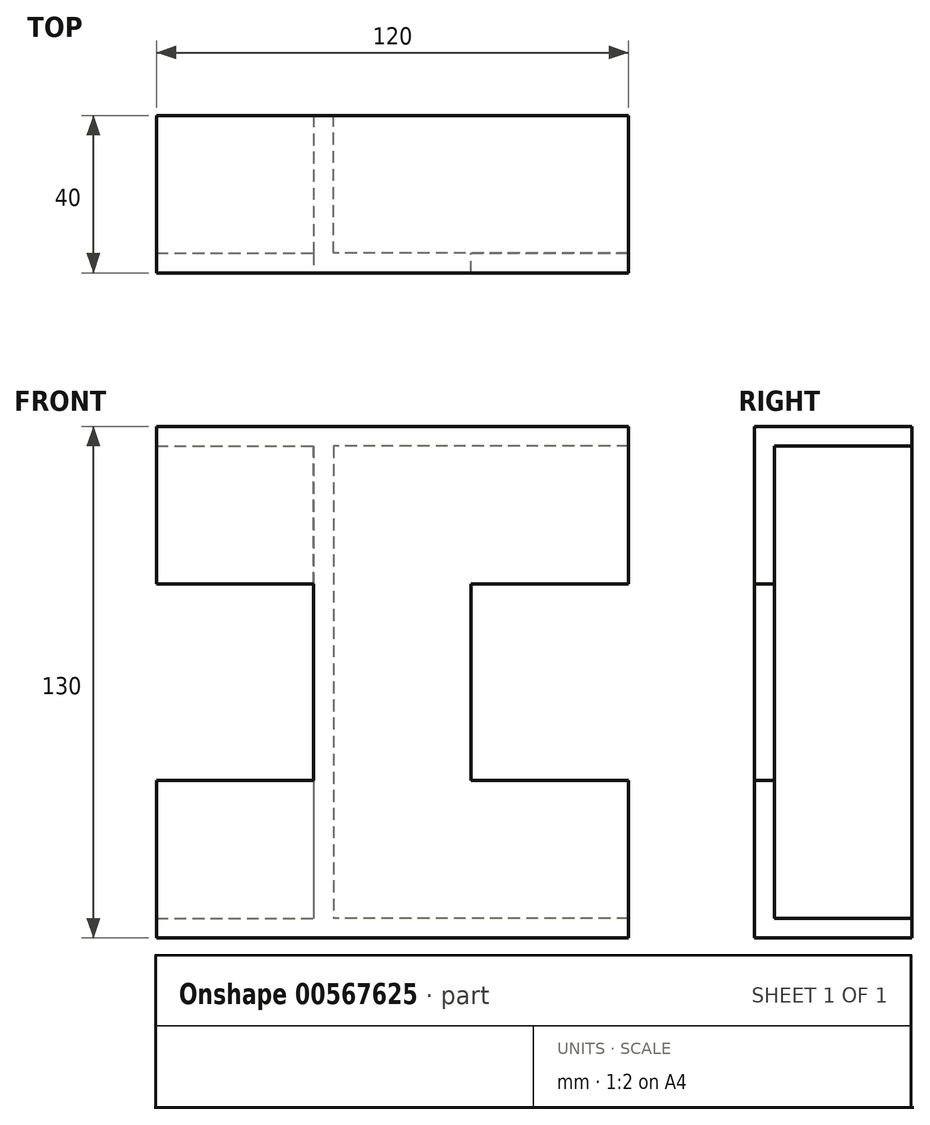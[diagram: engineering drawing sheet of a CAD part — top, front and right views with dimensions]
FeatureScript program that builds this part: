
annotation { "Feature Type Name" : "Feature", "Feature Type Description" : "" }
export const myFeature = defineFeature(function(context is Context, id is Id, definition is map)
    precondition{}
    {
        {
            var Q0;
            Q0=qCreatedBy(makeId("Right.planeOp"),FACE);
            var sketch = newSketch(context, id + "F0", { "sketchPlane" : qUnion([Q0])});
            skLineSegment(sketch, "E0", {"start": v(12.2, -34.52) * mm, "end": v(-27.8, -34.52) * mm});
            skLineSegment(sketch, "E1", {"start": v(-27.8, -34.52) * mm, "end": v(-27.8, -29.52) * mm});
            skLineSegment(sketch, "E2", {"start": v(-27.8, -29.52) * mm, "end": v(17.2, -29.52) * mm});
            skLineSegment(sketch, "E3", {"start": v(12.2, -34.52) * mm, "end": v(12.2, -29.52) * mm});
            skLineSegment(sketch, "E4", {"start": v(17.2, -29.52) * mm, "end": v(12.2, -29.52) * mm});
            skSolve(sketch);
        }
        {
            var Q0;
            Q0 = qSketchRegion(id + "F0", true);
            extrude(context, id + "F1", {"entities" : qUnion([Q0]), "depth" : 120 * mm, "offsetDistance" : 25 * mm});
        }
        {
            var Q0;
            Q0=makeQuery(id+"F1.opExtrude","SWEPT_FACE",FACE,{"disambiguationData":[OSD([sQuery(id+"F0.wireOp",EDGE,"E2"),sQuery(id+"F0.wireOp",EDGE,"E4")])]});
            var sketch = newSketch(context, id + "F2", { "sketchPlane" : qUnion([Q0])});
            skLineSegment(sketch, "E5", {"start": v(120, -27.8) * mm, "end": v(120, 12.2) * mm});
            skLineSegment(sketch, "E6", {"start": v(40, 12.2) * mm, "end": v(40, -27.8) * mm});
            skLineSegment(sketch, "E7", {"start": v(40, -27.8) * mm, "end": v(80, -27.8) * mm});
            skLineSegment(sketch, "E8", {"start": v(80, -27.8) * mm, "end": v(80, -22.8) * mm});
            skLineSegment(sketch, "E9", {"start": v(80, -22.8) * mm, "end": v(45, -22.8) * mm});
            skLineSegment(sketch, "E10", {"start": v(45, -22.8) * mm, "end": v(45, 12.2) * mm});
            skLineSegment(sketch, "E11", {"start": v(45, 12.2) * mm, "end": v(40, 12.2) * mm});
            skLineSegment(sketch, "E12", {"start": v(60, -27.8) * mm, "end": v(60, -7.8) * mm});
            skPoint(sketch, "E12.endSnap0", {"position": v(120, -7.8) * mm});
            skLineSegment(sketch, "E13", {"start": v(60, -7.8) * mm, "end": v(120, -7.8) * mm});
            skSolve(sketch);
        }
        {
            var Q0;
            Q0 = qSketchRegion(id + "F2", true);
            extrude(context, id + "F3", {"entities" : qUnion([Q0]), "operationType" : NewBodyOperationType.ADD, "depth" : 120 * mm, "offsetDistance" : 25 * mm});
        }
        {
            var Q0;
            Q0=makeQuery(id+"F3.opExtrude","CAP_FACE",FACE,{"disambiguationData":[OSD([sQuery(id+"F2.wireOp",EDGE,"E6"),sQuery(id+"F2.wireOp",EDGE,"E7"),sQuery(id+"F2.wireOp",EDGE,"E8"),sQuery(id+"F2.wireOp",EDGE,"E9"),sQuery(id+"F2.wireOp",EDGE,"E10"),sQuery(id+"F2.wireOp",EDGE,"E11")])],"isStart":false});
            var sketch = newSketch(context, id + "F4", { "sketchPlane" : qUnion([Q0])});
            skLineSegment(sketch, "E14.bottom", {"start": v(0, 12.2) * mm, "end": v(120, 12.2) * mm});
            skLineSegment(sketch, "E14.top", {"start": v(0, -27.8) * mm, "end": v(120, -27.8) * mm});
            skLineSegment(sketch, "E14.left", {"start": v(0, 12.2) * mm, "end": v(0, -27.8) * mm});
            skLineSegment(sketch, "E14.right", {"start": v(120, 12.2) * mm, "end": v(120, -27.8) * mm});
            skSolve(sketch);
        }
        {
            var Q0;
            Q0 = qSketchRegion(id + "F4", true);
            extrude(context, id + "F5", {"entities" : qUnion([Q0]), "operationType" : NewBodyOperationType.ADD, "depth" : 5 * mm, "offsetDistance" : 25 * mm});
        }
        {
            var Q0;
            {var subQ1=sQuery(id+"F0.wireOp",EDGE,"E4");var subQ2=sQuery(id+"F0.wireOp",EDGE,"E2");Q0=makeQuery(id+"F3.boolean.opBoolean","SPLIT",FACE,{"disambiguationData":[TD([makeQuery(id+"F3.opExtrude","SWEPT_FACE",FACE,{"disambiguationData":[OSD([sQuery(id+"F2.wireOp",EDGE,"E6")])]})])],"derivedFrom":makeQuery(id+"F1.opExtrude","SWEPT_FACE",FACE,{"disambiguationData":[OSD([subQ2,subQ1])]})});}
            var sketch = newSketch(context, id + "F6", { "sketchPlane" : qUnion([Q0])});
            skLineSegment(sketch, "E15", {"start": v(0, -27.8) * mm, "end": v(0, -22.8) * mm});
            skLineSegment(sketch, "E16", {"start": v(0, -22.8) * mm, "end": v(40, -22.8) * mm});
            skLineSegment(sketch, "E17", {"start": v(40, -22.8) * mm, "end": v(40, -27.8) * mm});
            skSolve(sketch);
        }
        {
            var Q0;
            Q0 = qSketchRegion(id + "F6", true);
            var Q1;
            Q1=makeQuery(id+"F6.imprint","IMPRINT",FACE,{"disambiguationData":[TD([[makeQuery(id+"F6.imprint","IMPRINT",EDGE,{"derivedFrom":sQuery(id+"F6.wireOp",EDGE,"E15")}),1.0]])]});
            var Q2;
            Q2=makeQuery(id+"F6.imprint","IMPRINT",FACE,{"disambiguationData":[TD([[makeQuery(id+"F6.imprint","IMPRINT",EDGE,{"derivedFrom":sQuery(id+"F6.wireOp",EDGE,"E15")}),-1.0]])]});
            extrude(context, id + "F7", {"entities" : qUnion([Q0, Q1, Q2]), "operationType" : NewBodyOperationType.ADD, "depth" : 35 * mm, "offsetDistance" : 25 * mm});
        }
        {
            var Q0;
            {var subQ2=sQuery(id+"F0.wireOp",EDGE,"E4");var subQ3=sQuery(id+"F0.wireOp",EDGE,"E2");Q0=makeQuery(id+"F3.boolean.opBoolean","SPLIT",FACE,{"disambiguationData":[TD([makeQuery(id+"F3.opExtrude","SWEPT_FACE",FACE,{"disambiguationData":[OSD([sQuery(id+"F2.wireOp",EDGE,"E8")])]})])],"derivedFrom":makeQuery(id+"F1.opExtrude","SWEPT_FACE",FACE,{"disambiguationData":[OSD([subQ3,subQ2])]})});}
            var sketch = newSketch(context, id + "F8", { "sketchPlane" : qUnion([Q0])});
            skLineSegment(sketch, "E18", {"start": v(80, -22.8) * mm, "end": v(120, -22.8) * mm});
            skSolve(sketch);
        }
        {
            var Q0;
            Q0 = qSketchRegion(id + "F8", true);
            var Q1;
            {var subQ0=sQuery(id+"F8.wireOp",EDGE,"E18");Q1=makeQuery(id+"F8.imprint","IMPRINT",FACE,{"disambiguationData":[TD([[makeQuery(id+"F8.imprint","IMPRINT",EDGE,{"derivedFrom":subQ0}),-1.0]])]});}
            extrude(context, id + "F9", {"entities" : qUnion([Q0, Q1]), "operationType" : NewBodyOperationType.ADD, "depth" : 35 * mm, "offsetDistance" : 25 * mm});
        }
        {
            var Q0;
            {var subQ0=sQuery(id+"F4.wireOp",EDGE,"E14.bottom");var subQ1=sQuery(id+"F4.wireOp",EDGE,"E14.top");var subQ2=sQuery(id+"F4.wireOp",EDGE,"E14.left");Q0=makeQuery(id+"F5.boolean.opBoolean","SPLIT",FACE,{"disambiguationData":[TD([makeQuery(id+"F3.opExtrude","SWEPT_FACE",FACE,{"disambiguationData":[OSD([sQuery(id+"F2.wireOp",EDGE,"E6")])]})])],"derivedFrom":makeQuery(id+"F5.opExtrude","CAP_FACE",FACE,{"disambiguationData":[OSD([subQ0,subQ1,subQ2,sQuery(id+"F4.wireOp",EDGE,"E14.right")])],"isStart":true})});}
            var sketch = newSketch(context, id + "F10", { "sketchPlane" : qUnion([Q0])});
            skLineSegment(sketch, "E19", {"start": v(0, 27.8) * mm, "end": v(0, 22.8) * mm});
            skLineSegment(sketch, "E20", {"start": v(0, 22.8) * mm, "end": v(40, 22.8) * mm});
            skSolve(sketch);
        }
        {
            var Q0;
            Q0 = qSketchRegion(id + "F10", true);
            var Q1;
            Q1=makeQuery(id+"F10.imprint","IMPRINT",FACE,{"disambiguationData":[TD([[makeQuery(id+"F10.imprint","IMPRINT",EDGE,{"derivedFrom":sQuery(id+"F10.wireOp",EDGE,"E19")}),-1.0]])]});
            extrude(context, id + "F11", {"entities" : qUnion([Q0, Q1]), "operationType" : NewBodyOperationType.ADD, "depth" : 35 * mm, "offsetDistance" : 25 * mm});
        }
        {
            var Q0;
            {var subQ0=sQuery(id+"F4.wireOp",EDGE,"E14.bottom");var subQ1=sQuery(id+"F4.wireOp",EDGE,"E14.top");var subQ2=sQuery(id+"F4.wireOp",EDGE,"E14.right");Q0=makeQuery(id+"F5.boolean.opBoolean","SPLIT",FACE,{"disambiguationData":[TD([makeQuery(id+"F3.opExtrude","SWEPT_FACE",FACE,{"disambiguationData":[OSD([sQuery(id+"F2.wireOp",EDGE,"E8")])]})])],"derivedFrom":makeQuery(id+"F5.opExtrude","CAP_FACE",FACE,{"disambiguationData":[OSD([subQ0,subQ1,sQuery(id+"F4.wireOp",EDGE,"E14.left"),subQ2])],"isStart":true})});}
            var sketch = newSketch(context, id + "F12", { "sketchPlane" : qUnion([Q0])});
            skLineSegment(sketch, "E21", {"start": v(80, 22.8) * mm, "end": v(120, 22.8) * mm});
            skSolve(sketch);
        }
        {
            var Q0;
            Q0 = qSketchRegion(id + "F12", true);
            var Q1;
            {var subQ0=sQuery(id+"F12.wireOp",EDGE,"E21");Q1=makeQuery(id+"F12.imprint","IMPRINT",FACE,{"disambiguationData":[TD([[makeQuery(id+"F12.imprint","IMPRINT",EDGE,{"derivedFrom":subQ0}),1.0]])]});}
            extrude(context, id + "F13", {"entities" : qUnion([Q0, Q1]), "operationType" : NewBodyOperationType.ADD, "depth" : 35 * mm, "offsetDistance" : 25 * mm});
        }
    });
